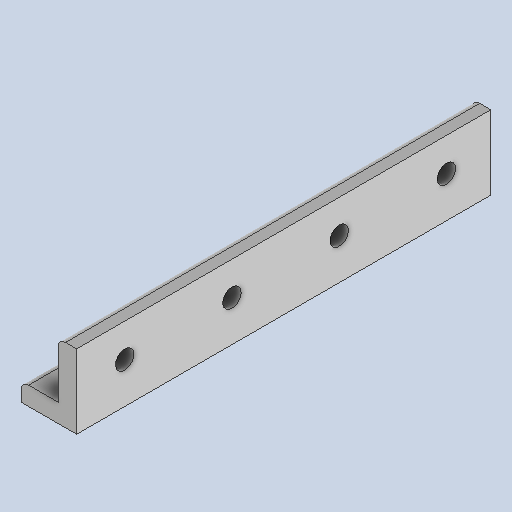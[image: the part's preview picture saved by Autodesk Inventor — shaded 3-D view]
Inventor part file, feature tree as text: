
AUTODESK INVENTOR PART (.ipt)
format: ipt  version: 2025.1 (Build 291241000, 241)  size: 116,224 bytes
history: native  units: mm
features: other x3, sketch x3
ambient origin geometry x8: Origin, YZ Plane, XZ Plane, XY Plane, X Axis, Y Axis, Z Axis, Center Point
bodies: Volumenkörper1 (feature_tree)
feature tree (6):
  other  "1014.ipt"
  other  "Volumenkörper1::1014.ipt"
  other  "TaggingFeature1"
  sketch  "Skizze2"  dims[d0=10.0mm]
  sketch  "Skizze3"
  sketch  "Skizze4"
